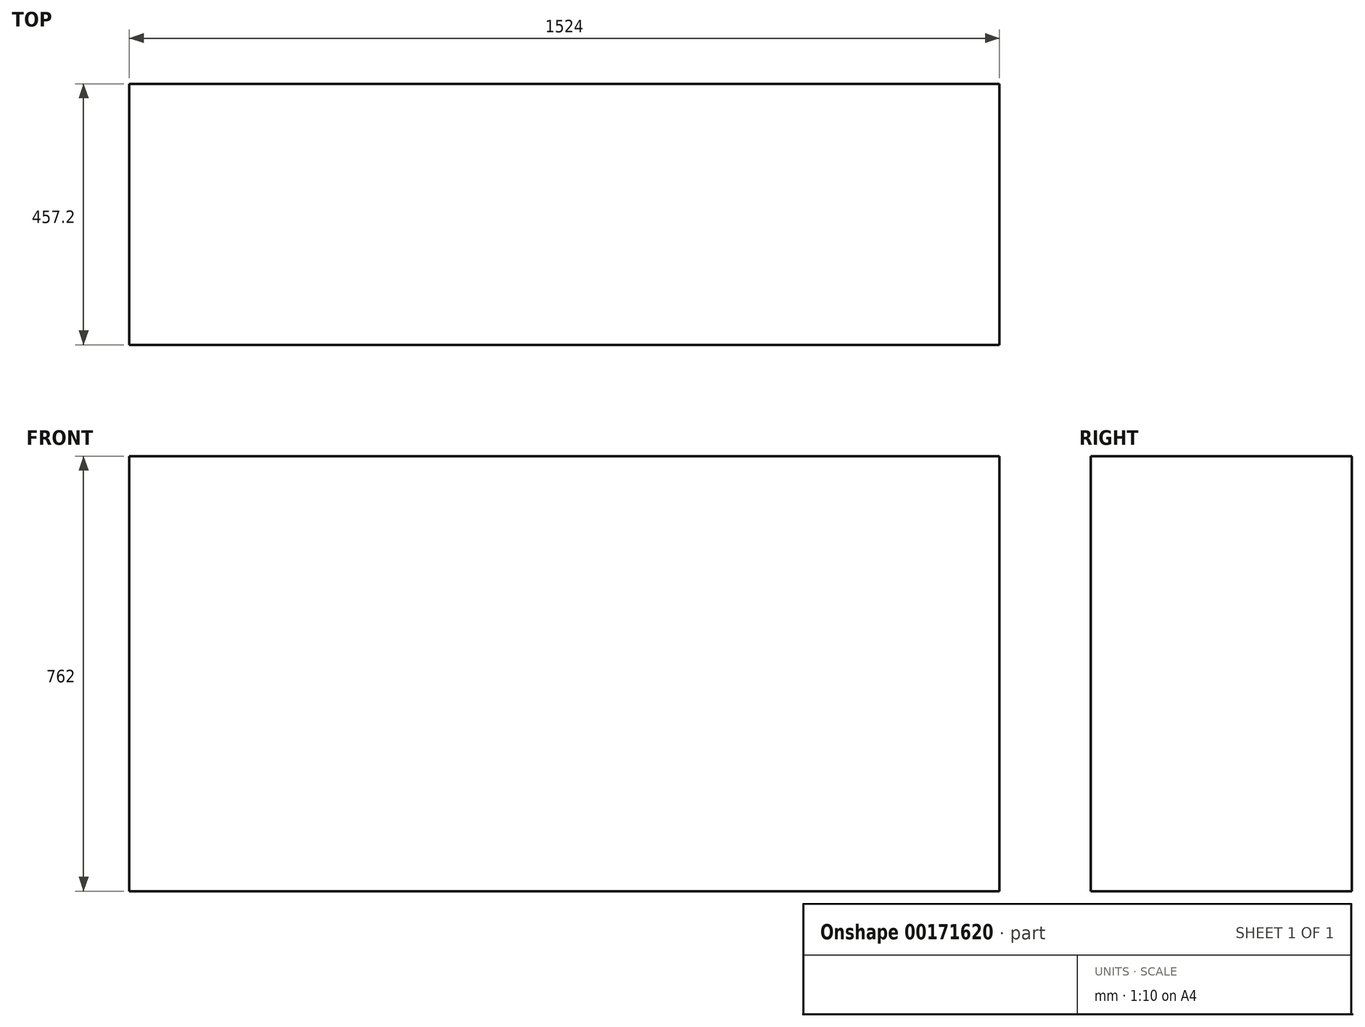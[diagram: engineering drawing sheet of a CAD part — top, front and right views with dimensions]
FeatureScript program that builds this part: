
annotation { "Feature Type Name" : "Feature", "Feature Type Description" : "" }
export const myFeature = defineFeature(function(context is Context, id is Id, definition is map)
    precondition{}
    {
        {
            var Q0;
            Q0=qCreatedBy(makeId("Top.planeOp"),FACE);
            var sketch = newSketch(context, id + "F0", { "sketchPlane" : qUnion([Q0])});
            skLineSegment(sketch, "E0.bottom", {"start": v(-108.68, -8.04) * mm, "end": v(1415.32, -8.04) * mm});
            skLineSegment(sketch, "E0.top", {"start": v(-108.68, 449.16) * mm, "end": v(1415.32, 449.16) * mm});
            skLineSegment(sketch, "E0.left", {"start": v(-108.68, -8.04) * mm, "end": v(-108.68, 449.16) * mm});
            skLineSegment(sketch, "E0.right", {"start": v(1415.32, -8.04) * mm, "end": v(1415.32, 449.16) * mm});
            skSolve(sketch);
        }
        {
            var Q0;
            Q0 = qSketchRegion(id + "F0", true);
            extrude(context, id + "F1", {"entities" : qUnion([Q0]), "depth" : 762 * mm});
        }
    });
